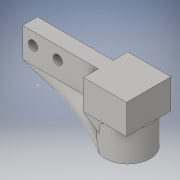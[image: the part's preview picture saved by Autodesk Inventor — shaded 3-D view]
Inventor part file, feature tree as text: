
AUTODESK INVENTOR PART (.ipt)
format: ipt  version: 2016 (Build 200138000, 138)  size: 196,608 bytes
history: native  units: in
note: dims shown in document units (in); Inventor stores cm internally (conversion verified against a paired STEP export)
features: sketch x6, extrude x4, other x2, hole x1, loft x1
ambient origin geometry x8: Origin, YZ Plane, XZ Plane, XY Plane, X Axis, Y Axis, Z Axis, Center Point
bodies: Solid1 (feature_tree)
feature tree (14):
  extrude  "Extrusion1"  Depth=0.5in
  hole  "Hole3"  [1 undecoded]
  extrude  "Extrusion2"  Depth=0.75in
  extrude  "Extrusion3"  Depth=0.25in TaperAngle=0.0deg
  extrude  "Extrusion5"  TaperAngle=0.0deg  [1 undecoded]
  loft  "Loft2"
  sketch  "Sketch7"  dims[d48=0.25in d49=0.0in d50=0.0in d51=90.0deg d52=0.0in d53=90.0deg d4=1.0in d5=1.0in]
  sketch  "Sketch1"  dims[d0=2.0in d1=0.5in]
  sketch  "Sketch2"  dims[d2=0.25in d3=0.0in d22=0.1575in]
  sketch  "Sketch3"  dims[d23=0.7874in d25=0.4173in d26=0.3937in d28=1.0in]
  sketch  "Sketch4"  dims[d30=0.1575in d31=0.75in d32=0.375in d33=0.25in d34=0.5635in d35=0.1575in d36=0.8108in d37=0.75in]
  sketch  "Sketch6"  dims[d38=0.5in d39=0.0in d40=0.25in d41=0.0in]
  other  "Edges3"
  other  "Edges4"
note: 2 required parameter values undecoded (feature->parameter linkage not recoverable at this tier; creation-order binding heuristic only, values carry confidence <= 0.55)
